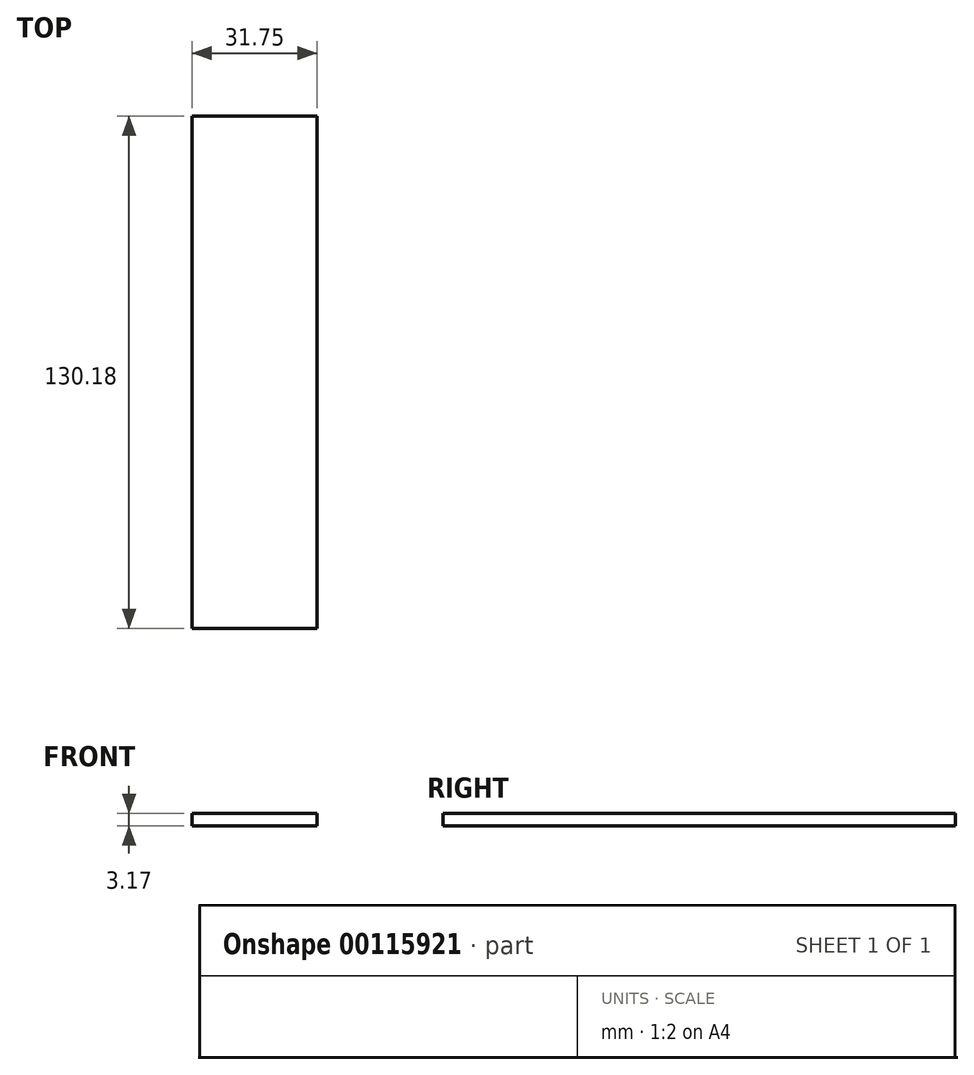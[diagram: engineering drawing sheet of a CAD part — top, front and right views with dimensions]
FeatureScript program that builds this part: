
annotation { "Feature Type Name" : "Feature", "Feature Type Description" : "" }
export const myFeature = defineFeature(function(context is Context, id is Id, definition is map)
    precondition{}
    {
        {
            var Q0;
            Q0=qCreatedBy(makeId("Top.planeOp"),FACE);
            var sketch = newSketch(context, id + "F0", { "sketchPlane" : qUnion([Q0])});
            skLineSegment(sketch, "E0.bottom", {"start": v(-73.62, 61.27) * mm, "end": v(-41.87, 61.27) * mm});
            skLineSegment(sketch, "E0.top", {"start": v(-73.62, -68.9) * mm, "end": v(-41.87, -68.9) * mm});
            skLineSegment(sketch, "E0.left", {"start": v(-73.62, 61.27) * mm, "end": v(-73.62, -68.9) * mm});
            skLineSegment(sketch, "E0.right", {"start": v(-41.87, 61.27) * mm, "end": v(-41.87, -68.9) * mm});
            skSolve(sketch);
        }
        {
            var Q0;
            Q0=makeQuery(id+"F0.imprint","IMPRINT",FACE,{"disambiguationData":[TD([[makeQuery(id+"F0.imprint","IMPRINT",EDGE,{"derivedFrom":sQuery(id+"F0.wireOp",EDGE,"E0.bottom")}),-1.0]])]});
            extrude(context, id + "F1", {"entities" : qUnion([Q0]), "depth" : 3.17 * mm});
        }
    });
